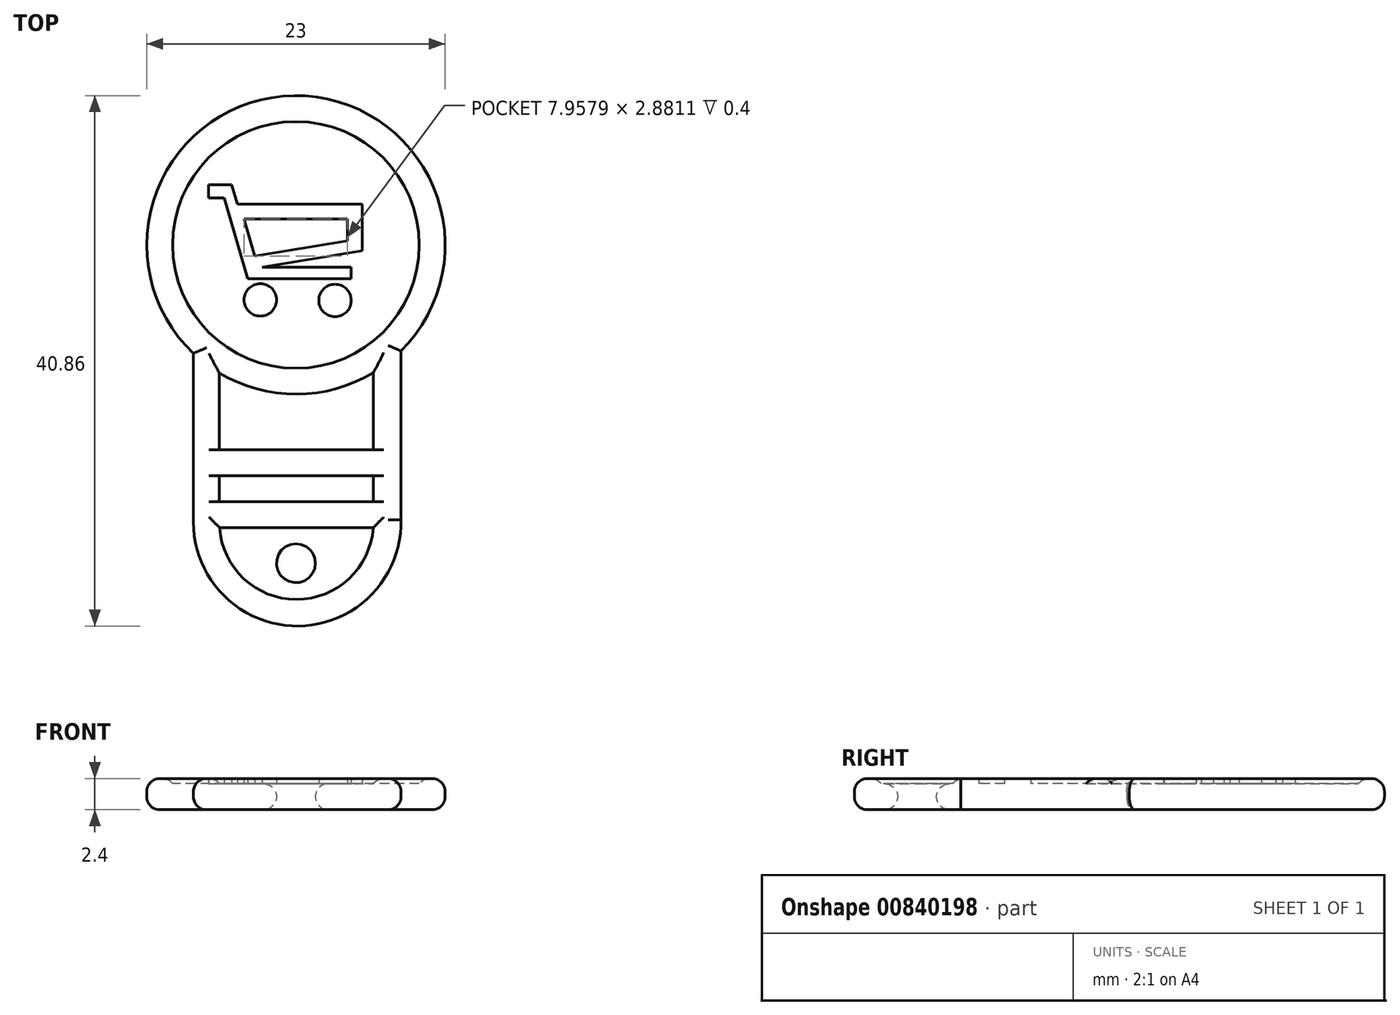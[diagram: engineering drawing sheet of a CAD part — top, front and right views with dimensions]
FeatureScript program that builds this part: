
annotation { "Feature Type Name" : "Feature", "Feature Type Description" : "" }
export const myFeature = defineFeature(function(context is Context, id is Id, definition is map)
    precondition{}
    {
        {
            var Q0;
            Q0=qCreatedBy(makeId("Top.planeOp"),FACE);
            var sketch = newSketch(context, id + "F0", { "sketchPlane" : qUnion([Q0])});
            skCircle(sketch, "E0", {"center": v(0, 0) * mm, "radius": 11.5 * mm});
            skLineSegment(sketch, "E1", {"start": v(-7.9, -8.36) * mm, "end": v(-7.9, -21.36) * mm});
            skLineSegment(sketch, "E2", {"start": v(8.1, -8.17) * mm, "end": v(8.1, -21.17) * mm});
            skArc(sketch, "E3", {"start": v(-7.9, -21.36) * mm, "mid": v(0.2, -29.35) * mm, "end": v(8.1, -21.17) * mm});
            skPoint(sketch, "E4.trimOffspring.end.orphan", {"position": v(0.2, -29.35) * mm});
            skCircle(sketch, "E5", {"center": v(0, -24.52) * mm, "radius": 1.5 * mm});
            skSolve(sketch);
        }
        {
            var Q0;
            {var subQ0=sQuery(id+"F0.wireOp",EDGE,"E0");var subQ1=makeQuery(id+"F0.imprint","INTERSECT",VERTEX,{"derivedFrom":[subQ0,sQuery(id+"F0.wireOp",EDGE,"E1")]});Q0=makeQuery(id+"F0.imprint","IMPRINT",FACE,{"disambiguationData":[TD([[makeQuery(id+"F0.imprint","IMPRINT",EDGE,{"disambiguationData":[TD([[subQ1,-1.0]])],"derivedFrom":subQ0}),1.0]])]});}
            var Q1;
            {var subQ1=sQuery(id+"F0.wireOp",EDGE,"E1");Q1=makeQuery(id+"F0.imprint","IMPRINT",FACE,{"disambiguationData":[TD([[makeQuery(id+"F0.imprint","IMPRINT",EDGE,{"derivedFrom":subQ1}),1.0]])]});}
            extrude(context, id + "F1", {"entities" : qUnion([Q0, Q1]), "depth" : 2 * mm, "offsetDistance" : 25 * mm});
        }
        {
            var Q0;
            Q0=makeQuery(id+"F1.opExtrude","CAP_FACE",FACE,{"disambiguationData":[OSD([sQuery(id+"F0.wireOp",EDGE,"E0"),sQuery(id+"F0.wireOp",EDGE,"E1"),sQuery(id+"F0.wireOp",EDGE,"E2"),sQuery(id+"F0.wireOp",EDGE,"E3"),sQuery(id+"F0.wireOp",EDGE,"fh5twboJ-bka2-FRvl-eJyA-GtjpmXtnkDHU")])],"isStart":false});
            var sketch = newSketch(context, id + "F2", { "sketchPlane" : qUnion([Q0])});
            skCircle(sketch, "E6", {"center": v(0, 0) * mm, "radius": 11.5 * mm});
            skCircle(sketch, "E7", {"center": v(0, 0) * mm, "radius": 9.5 * mm});
            skSolve(sketch);
        }
        {
            var Q0;
            Q0=makeQuery(id+"F2.imprint","IMPRINT",FACE,{"disambiguationData":[TD([[makeQuery(id+"F2.imprint","IMPRINT",EDGE,{"derivedFrom":sQuery(id+"F2.wireOp",EDGE,"E7")}),-1.0]])]});
            extrude(context, id + "F3", {"entities" : qUnion([Q0]), "operationType" : NewBodyOperationType.ADD, "depth" : .4 * mm, "offsetDistance" : 25 * mm});
        }
        {
            var Q0;
            {var subQ0=sQuery(id+"F0.wireOp",EDGE,"E2");var subQ1=sQuery(id+"F0.wireOp",EDGE,"E1");var subQ2=sQuery(id+"F0.wireOp",EDGE,"E3");var subQ3=sQuery(id+"F0.wireOp",EDGE,"E0");var subQ4=sQuery(id+"F0.wireOp",EDGE,"fh5twboJ-bka2-FRvl-eJyA-GtjpmXtnkDHU");Q0=makeQuery(id+"F3.boolean.opBoolean","SPLIT",FACE,{"disambiguationData":[TD([makeQuery(id+"F1.opExtrude","SWEPT_FACE",FACE,{"disambiguationData":[OSD([subQ3])]})])],"derivedFrom":makeQuery(id+"F1.opExtrude","CAP_FACE",FACE,{"disambiguationData":[OSD([subQ3,subQ1,subQ0,subQ2,subQ4])],"isStart":false})});}
            var sketch = newSketch(context, id + "F4", { "sketchPlane" : qUnion([Q0])});
            skLineSegment(sketch, "E8", {"start": v(-5.9, -9.87) * mm, "end": v(-5.9, -21.37) * mm});
            skPoint(sketch, "E9.center.orphan", {"position": v(0, -28.91) * mm});
            skLineSegment(sketch, "E10", {"start": v(5.97, -9.83) * mm, "end": v(5.97, -21.33) * mm});
            skArc(sketch, "E11", {"start": v(-5.9, -21.37) * mm, "mid": v(0.06, -27.3) * mm, "end": v(5.97, -21.33) * mm});
            skPoint(sketch, "E12.endSnap0", {"position": v(5.97, -15.58) * mm});
            skPoint(sketch, "E13.end.orphan", {"position": v(5.97, -28.7) * mm});
            skLineSegment(sketch, "E14", {"start": v(-5.9, -19.77) * mm, "end": v(5.97, -19.77) * mm});
            skLineSegment(sketch, "E15", {"start": v(-5.9, -21.77) * mm, "end": v(5.97, -21.77) * mm});
            skPoint(sketch, "E12.end.orphan", {"position": v(5.97, -12.77) * mm});
            skLineSegment(sketch, "E16", {"start": v(-5.9, -17.77) * mm, "end": v(5.97, -17.77) * mm});
            skLineSegment(sketch, "E17", {"start": v(-5.9, -15.77) * mm, "end": v(5.97, -15.77) * mm});
            skSolve(sketch);
        }
        {
            var Q0;
            {var subQ0=sQuery(id+"F4.wireOp",EDGE,"E11");Q0=makeQuery(id+"F4.imprint","IMPRINT",FACE,{"disambiguationData":[TD([[makeQuery(id+"F4.imprint","IMPRINT",EDGE,{"derivedFrom":subQ0}),-1.0]])]});}
            var Q1;
            {var subQ0=sQuery(id+"F4.wireOp",EDGE,"E16");Q1=makeQuery(id+"F4.imprint","IMPRINT",FACE,{"disambiguationData":[TD([[makeQuery(id+"F4.imprint","IMPRINT",EDGE,{"derivedFrom":subQ0}),1.0]])]});}
            var Q2;
            {var subQ0=sQuery(id+"F4.wireOp",EDGE,"E14");Q2=makeQuery(id+"F4.imprint","IMPRINT",FACE,{"disambiguationData":[TD([[makeQuery(id+"F4.imprint","IMPRINT",EDGE,{"derivedFrom":subQ0}),-1.0]])]});}
            extrude(context, id + "F5", {"entities" : qUnion([Q0, Q1, Q2]), "operationType" : NewBodyOperationType.ADD, "depth" : .4 * mm, "offsetDistance" : 25 * mm});
        }
        {
            var Q0;
            Q0=makeQuery(id+"F3.boolean.opBoolean","SPLIT",FACE,{"disambiguationData":[TD([makeQuery(id+"F3.opExtrude","SWEPT_FACE",FACE,{"disambiguationData":[OSD([sQuery(id+"F2.wireOp",EDGE,"E7")])]})])],"derivedFrom":makeQuery(id+"F1.opExtrude","CAP_FACE",FACE,{"disambiguationData":[OSD([sQuery(id+"F0.wireOp",EDGE,"E0"),sQuery(id+"F0.wireOp",EDGE,"E1"),sQuery(id+"F0.wireOp",EDGE,"E2"),sQuery(id+"F0.wireOp",EDGE,"E3")])],"isStart":false})});
            var sketch = newSketch(context, id + "F6", { "sketchPlane" : qUnion([Q0])});
            skLineSegment(sketch, "E18", {"start": v(-6.74, 4.62) * mm, "end": v(-4.95, 4.62) * mm});
            skLineSegment(sketch, "E19", {"start": v(-4.95, 4.62) * mm, "end": v(-4.52, 3.13) * mm});
            skLineSegment(sketch, "E20", {"start": v(-2.6, -1.7) * mm, "end": v(4.26, -1.7) * mm});
            skLineSegment(sketch, "E21", {"start": v(4.26, -1.7) * mm, "end": v(4.26, -2.61) * mm});
            skLineSegment(sketch, "E22", {"start": v(4.26, -2.61) * mm, "end": v(-3.73, -2.61) * mm});
            skLineSegment(sketch, "E23", {"start": v(-3.73, -2.61) * mm, "end": v(-5.53, 3.63) * mm});
            skLineSegment(sketch, "E24", {"start": v(-5.53, 3.63) * mm, "end": v(-6.74, 3.63) * mm});
            skLineSegment(sketch, "E25", {"start": v(-6.74, 3.63) * mm, "end": v(-6.74, 4.62) * mm});
            skLineSegment(sketch, "E26", {"start": v(-4.52, 3.13) * mm, "end": v(5.1, 3.13) * mm});
            skLineSegment(sketch, "E27", {"start": v(5.1, 3.13) * mm, "end": v(5.1, -0.43) * mm});
            skLineSegment(sketch, "E28", {"start": v(5.1, -0.43) * mm, "end": v(-2.6, -1.7) * mm});
            skLineSegment(sketch, "E29", {"start": v(-4, 2.01) * mm, "end": v(3.96, 2.01) * mm});
            skLineSegment(sketch, "E30", {"start": v(3.96, 2.01) * mm, "end": v(3.96, 0.31) * mm});
            skLineSegment(sketch, "E31", {"start": v(-3.17, -0.87) * mm, "end": v(-4, 2.01) * mm});
            skCircle(sketch, "E32", {"center": v(-2.74, -4.23) * mm, "radius": 1.25 * mm});
            skCircle(sketch, "E33", {"center": v(3.01, -4.28) * mm, "radius": 1.25 * mm});
            skLineSegment(sketch, "E34", {"start": v(3.96, 0.31) * mm, "end": v(-3.17, -0.87) * mm});
            skSolve(sketch);
        }
        {
            var Q0;
            Q0=makeQuery(id+"F6.imprint","IMPRINT",FACE,{"disambiguationData":[TD([[makeQuery(id+"F6.imprint","IMPRINT",EDGE,{"derivedFrom":sQuery(id+"F6.wireOp",EDGE,"E18")}),-1.0]])]});
            var Q1;
            Q1=makeQuery(id+"F6.imprint","IMPRINT",FACE,{"disambiguationData":[TD([[makeQuery(id+"F6.imprint","IMPRINT",EDGE,{"derivedFrom":sQuery(id+"F6.wireOp",EDGE,"E32")}),1.0]])]});
            var Q2;
            Q2=makeQuery(id+"F6.imprint","IMPRINT",FACE,{"disambiguationData":[TD([[makeQuery(id+"F6.imprint","IMPRINT",EDGE,{"derivedFrom":sQuery(id+"F6.wireOp",EDGE,"E33")}),1.0]])]});
            extrude(context, id + "F7", {"entities" : qUnion([Q0, Q1, Q2]), "operationType" : NewBodyOperationType.ADD, "depth" : .4 * mm, "offsetDistance" : 25 * mm});
        }
        {
            var Q0;
            Q0=makeQuery(id+"F3.opExtrude","CAP_EDGE",EDGE,{"disambiguationData":[OSD([sQuery(id+"F2.wireOp",EDGE,"E7")])],"isStart":false});
            var Q1;
            {var subQ1=sQuery(id+"F2.wireOp",EDGE,"E6");var subQ2=sQuery(id+"F0.wireOp",EDGE,"E1");Q1=makeQuery(id+"F5.boolean.opBoolean","SPLIT",EDGE,{"disambiguationData":[TD([makeQuery(id+"F1.opExtrude","SWEPT_FACE",FACE,{"disambiguationData":[OSD([subQ2])]})])],"derivedFrom":makeQuery(id+"F3.opExtrude","CAP_EDGE",EDGE,{"disambiguationData":[OSD([subQ1])],"isStart":false})});}
            var Q2;
            Q2=makeQuery(id+"F5.opExtrude","CAP_EDGE",EDGE,{"disambiguationData":[OSD([sQuery(id+"F0.wireOp",EDGE,"E2")])],"isStart":false});
            var Q3;
            Q3=makeQuery(id+"F5.opExtrude","CAP_EDGE",EDGE,{"disambiguationData":[OSD([sQuery(id+"F0.wireOp",EDGE,"E3")])],"isStart":false});
            var Q4;
            Q4=makeQuery(id+"F1.opExtrude","CAP_EDGE",EDGE,{"disambiguationData":[OSD([sQuery(id+"F0.wireOp",EDGE,"E1")])],"isStart":true});
            var Q5;
            Q5=makeQuery(id+"F1.opExtrude","CAP_EDGE",EDGE,{"disambiguationData":[OSD([sQuery(id+"F0.wireOp",EDGE,"E0")])],"isStart":true});
            var Q6;
            {var subQ0=sQuery(id+"F4.wireOp",EDGE,"E10");Q6=makeQuery(id+"F5.opExtrude","CAP_EDGE",EDGE,{"disambiguationData":[OSD([subQ0]),TDD([makeQuery(id+"F4.imprint","IMPRINT",EDGE,{"disambiguationData":[TD([[makeQuery(id+"F4.imprint","INTERSECT",VERTEX,{"derivedFrom":[makeQuery(id+"F3.opExtrude","CAP_EDGE",EDGE,{"disambiguationData":[OSD([sQuery(id+"F2.wireOp",EDGE,"E6")])],"isStart":true}),subQ0]}),-1.0]])],"derivedFrom":subQ0})])],"isStart":false});}
            var Q7;
            {var subQ0=sQuery(id+"F4.wireOp",EDGE,"E8");var subQ1=sQuery(id+"F2.wireOp",EDGE,"E6");var subQ2=makeQuery(id+"F3.opExtrude","CAP_EDGE",EDGE,{"disambiguationData":[OSD([subQ1])],"isStart":true});Q7=makeQuery(id+"F5.boolean.opBoolean","SPLIT",EDGE,{"disambiguationData":[TD([makeQuery(id+"F5.opExtrude","SWEPT_FACE",FACE,{"disambiguationData":[OSD([subQ0]),TDD([makeQuery(id+"F4.imprint","IMPRINT",EDGE,{"disambiguationData":[TD([[makeQuery(id+"F4.imprint","INTERSECT",VERTEX,{"derivedFrom":[subQ2,subQ0]}),-1.0]])],"derivedFrom":subQ0})])]})])],"derivedFrom":makeQuery(id+"F3.opExtrude","CAP_EDGE",EDGE,{"disambiguationData":[OSD([subQ1])],"isStart":false})});}
            var Q8;
            {var subQ0=sQuery(id+"F4.wireOp",EDGE,"E8");Q8=makeQuery(id+"F5.opExtrude","CAP_EDGE",EDGE,{"disambiguationData":[OSD([subQ0]),TDD([makeQuery(id+"F4.imprint","IMPRINT",EDGE,{"disambiguationData":[TD([[makeQuery(id+"F4.imprint","INTERSECT",VERTEX,{"derivedFrom":[makeQuery(id+"F3.opExtrude","CAP_EDGE",EDGE,{"disambiguationData":[OSD([sQuery(id+"F2.wireOp",EDGE,"E6")])],"isStart":true}),subQ0]}),-1.0]])],"derivedFrom":subQ0})])],"isStart":false});}
            var Q9;
            Q9=makeQuery(id+"F1.opExtrude","CAP_EDGE",EDGE,{"disambiguationData":[OSD([sQuery(id+"F0.wireOp",EDGE,"E5")])],"isStart":false});
            var Q10;
            Q10=makeQuery(id+"F1.opExtrude","CAP_EDGE",EDGE,{"disambiguationData":[OSD([sQuery(id+"F0.wireOp",EDGE,"E5")])],"isStart":true});
            var Q11;
            {var subQ0=sQuery(id+"F4.wireOp",EDGE,"E8");Q11=makeQuery(id+"F5.opExtrude","CAP_EDGE",EDGE,{"disambiguationData":[OSD([subQ0]),TDD([makeQuery(id+"F4.imprint","IMPRINT",EDGE,{"disambiguationData":[TD([[makeQuery(id+"F4.imprint","INTERSECT",VERTEX,{"derivedFrom":[subQ0,sQuery(id+"F4.wireOp",EDGE,"E14")]}),1.0]])],"derivedFrom":subQ0})])],"isStart":false});}
            var Q12;
            {var subQ0=sQuery(id+"F4.wireOp",EDGE,"E10");Q12=makeQuery(id+"F5.opExtrude","CAP_EDGE",EDGE,{"disambiguationData":[OSD([subQ0]),TDD([makeQuery(id+"F4.imprint","IMPRINT",EDGE,{"disambiguationData":[TD([[makeQuery(id+"F4.imprint","INTERSECT",VERTEX,{"derivedFrom":[subQ0,sQuery(id+"F4.wireOp",EDGE,"E14")]}),1.0]])],"derivedFrom":subQ0})])],"isStart":false});}
            var Q13;
            Q13=makeQuery(id+"F5.opExtrude","CAP_EDGE",EDGE,{"disambiguationData":[OSD([sQuery(id+"F4.wireOp",EDGE,"E11")])],"isStart":false});
            var Q14;
            Q14=makeQuery(id+"F5.opExtrude","CAP_EDGE",EDGE,{"disambiguationData":[OSD([sQuery(id+"F4.wireOp",EDGE,"E15")])],"isStart":false});
            fillet(context, id + "F8", {"entities" : qUnion([Q0, Q1, Q2, Q3, Q4, Q5, Q6, Q7, Q8, Q9, Q10, Q11, Q12, Q13, Q14]), "radius" : 1 * mm, "tangentPropagation" : true, "allowEdgeOverflow" : false});
        }
    });
